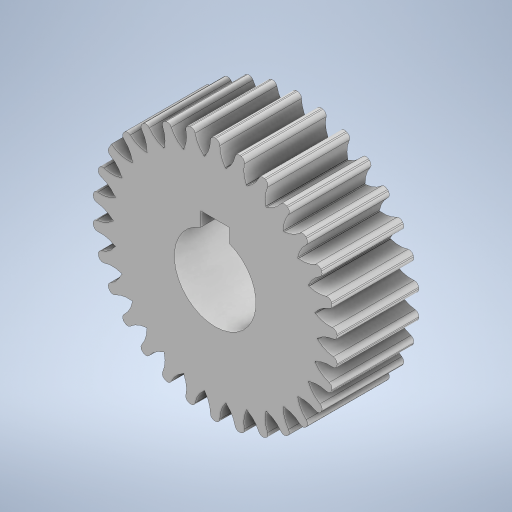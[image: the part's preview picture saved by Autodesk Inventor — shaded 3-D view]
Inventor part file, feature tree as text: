
AUTODESK INVENTOR PART (.ipt)
format: ipt  version: 2024 (Build 280153000, 153)  size: 665,088 bytes
history: native  units: mm
features: extrude x3, sketch x3, fillet x1
ambient origin geometry x8: Origin, YZ Plane, XZ Plane, XY Plane, X Axis, Y Axis, Z Axis, Center Point
bodies: Solid1 (feature_tree)
feature tree (7):
  extrude  "Extrusion1"  Depth=5.0mm
  fillet  "Fillet1"  Radius=300.0mm
  extrude  "Extrusion2"  Depth=1.0mm
  extrude  "Extrusion3"  TaperAngle=0.0deg  [1 undecoded]
  sketch  "Sketch1"  dims[d0=50.0mm d1=5.0mm d3=300.0mm d5=360.0deg]
  sketch  "Sketch2"  dims[d7=20.0mm d8=0.0mm d9=1.0mm]
  sketch  "Sketch3"  dims[d10=20.0mm d11=0.0mm d12=0.0mm d15=0.0mm d16=0.0mm d17=7.0mm d18=5.63mm d19=0.5mm d20=0.872665mm d21=0.5mm d22=0.872665mm]
note: 1 required parameter value undecoded (feature->parameter linkage not recoverable at this tier; creation-order binding heuristic only, values carry confidence <= 0.55)
